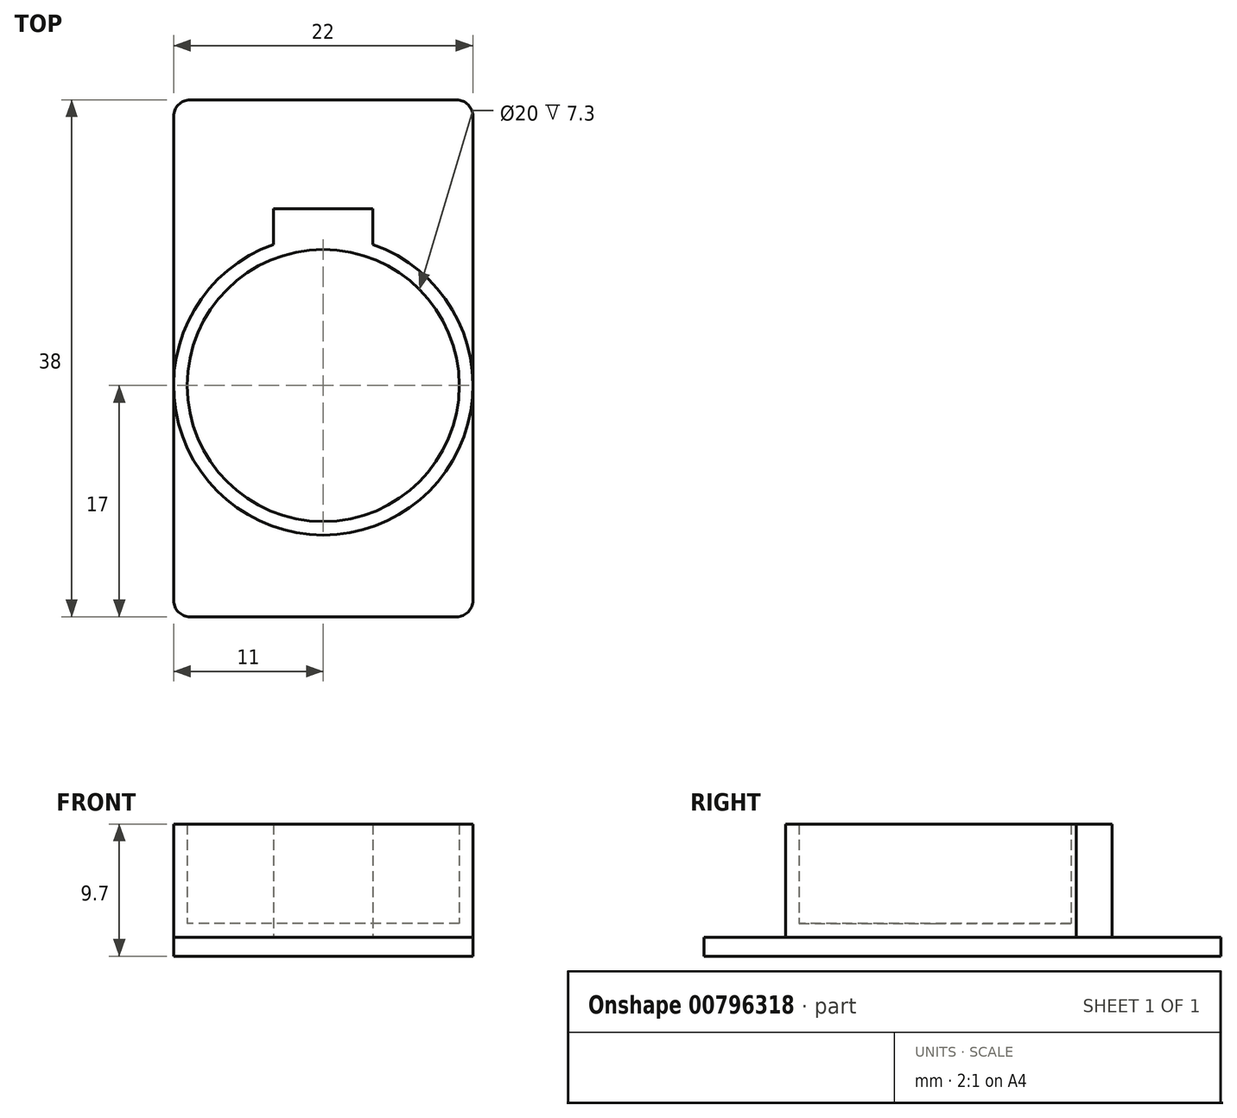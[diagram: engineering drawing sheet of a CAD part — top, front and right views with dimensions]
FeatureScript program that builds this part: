
annotation { "Feature Type Name" : "Feature", "Feature Type Description" : "" }
export const myFeature = defineFeature(function(context is Context, id is Id, definition is map)
    precondition{}
    {
        {
            var Q0;
            Q0=qCreatedBy(makeId("Top.planeOp"),FACE);
            var sketch = newSketch(context, id + "F0", { "sketchPlane" : qUnion([Q0])});
            skLineSegment(sketch, "E0.bottom", {"start": v(11, 19) * mm, "end": v(-11, 19) * mm});
            skLineSegment(sketch, "E0.top", {"start": v(11, -19) * mm, "end": v(-11, -19) * mm});
            skLineSegment(sketch, "E0.left", {"start": v(11, 19) * mm, "end": v(11, -19) * mm});
            skLineSegment(sketch, "E0.right", {"start": v(-11, 19) * mm, "end": v(-11, -19) * mm});
            skPoint(sketch, "E0.middle", {"position": v(0, 0) * mm});
            skSolve(sketch);
        }
        {
            var Q0;
            Q0=makeQuery(id+"F0.imprint","IMPRINT",FACE,{"disambiguationData":[TD([[makeQuery(id+"F0.imprint","IMPRINT",EDGE,{"derivedFrom":sQuery(id+"F0.wireOp",EDGE,"E0.bottom")}),1.0]])]});
            extrude(context, id + "F1", {"entities" : qUnion([Q0]), "depth" : 1.4 * mm, "offsetDistance" : 25 * mm});
        }
        {
            var Q0;
            Q0=makeQuery(id+"F1.opExtrude","SWEPT_EDGE",EDGE,{"disambiguationData":[OSD([sQuery(id+"F0.wireOp",EDGE,"E0.bottom"),sQuery(id+"F0.wireOp",EDGE,"E0.right")])]});
            var Q1;
            Q1=makeQuery(id+"F1.opExtrude","SWEPT_EDGE",EDGE,{"disambiguationData":[OSD([sQuery(id+"F0.wireOp",EDGE,"E0.bottom"),sQuery(id+"F0.wireOp",EDGE,"E0.left")])]});
            var Q2;
            Q2=makeQuery(id+"F1.opExtrude","SWEPT_EDGE",EDGE,{"disambiguationData":[OSD([sQuery(id+"F0.wireOp",EDGE,"E0.top"),sQuery(id+"F0.wireOp",EDGE,"E0.right")])]});
            var Q3;
            Q3=makeQuery(id+"F1.opExtrude","SWEPT_EDGE",EDGE,{"disambiguationData":[OSD([sQuery(id+"F0.wireOp",EDGE,"E0.top"),sQuery(id+"F0.wireOp",EDGE,"E0.left")])]});
            fillet(context, id + "F2", {"entities" : qUnion([Q0, Q1, Q2, Q3]), "radius" : 1.2 * mm, "tangentPropagation" : true, "allowEdgeOverflow" : false});
        }
        {
            var Q0;
            Q0=makeQuery(id+"F1.opExtrude","CAP_FACE",FACE,{"disambiguationData":[OSD([sQuery(id+"F0.wireOp",EDGE,"E0.bottom"),sQuery(id+"F0.wireOp",EDGE,"E0.top"),sQuery(id+"F0.wireOp",EDGE,"E0.left"),sQuery(id+"F0.wireOp",EDGE,"E0.right")])],"isStart":false});
            var sketch = newSketch(context, id + "F3", { "sketchPlane" : qUnion([Q0])});
            skLineSegment(sketch, "E1", {"start": v(0, 0.56) * mm, "end": v(0, -22.69) * mm, "construction": true});
            skPoint(sketch, "E1.endSnap0", {"position": v(0, -19) * mm});
            skCircle(sketch, "E2", {"center": v(0, -2) * mm, "radius": 11 * mm});
            skCircle(sketch, "E3", {"center": v(0, -2) * mm, "radius": 10 * mm});
            skLineSegment(sketch, "E4", {"start": v(0, 0.56) * mm, "end": v(0, 14.37) * mm, "construction": true});
            skLineSegment(sketch, "E5.bottom", {"start": v(-3.65, 8.38) * mm, "end": v(3.65, 8.38) * mm});
            skLineSegment(sketch, "E5.top", {"start": v(-3.65, 11) * mm, "end": v(3.65, 11) * mm});
            skLineSegment(sketch, "E5.left", {"start": v(-3.65, 8.38) * mm, "end": v(-3.65, 11) * mm});
            skLineSegment(sketch, "E5.right", {"start": v(3.65, 8.38) * mm, "end": v(3.65, 11) * mm});
            skPoint(sketch, "E5.middle", {"position": v(0, 9.69) * mm});
            skSolve(sketch);
        }
        {
            var Q0;
            Q0 = qSketchRegion(id + "F3", true);
            extrude(context, id + "F4", {"entities" : qUnion([Q0]), "depth" : 8.3 * mm, "offsetDistance" : 25 * mm});
        }
        {
            var Q0;
            Q0=makeQuery(id+"F3.imprint","IMPRINT",FACE,{"disambiguationData":[TD([[makeQuery(id+"F3.imprint","IMPRINT",EDGE,{"derivedFrom":sQuery(id+"F3.wireOp",EDGE,"E3")}),1.0]])]});
            extrude(context, id + "F5", {"entities" : qUnion([Q0]), "operationType" : NewBodyOperationType.ADD, "depth" : 1 * mm, "offsetDistance" : 25 * mm});
        }
    });
